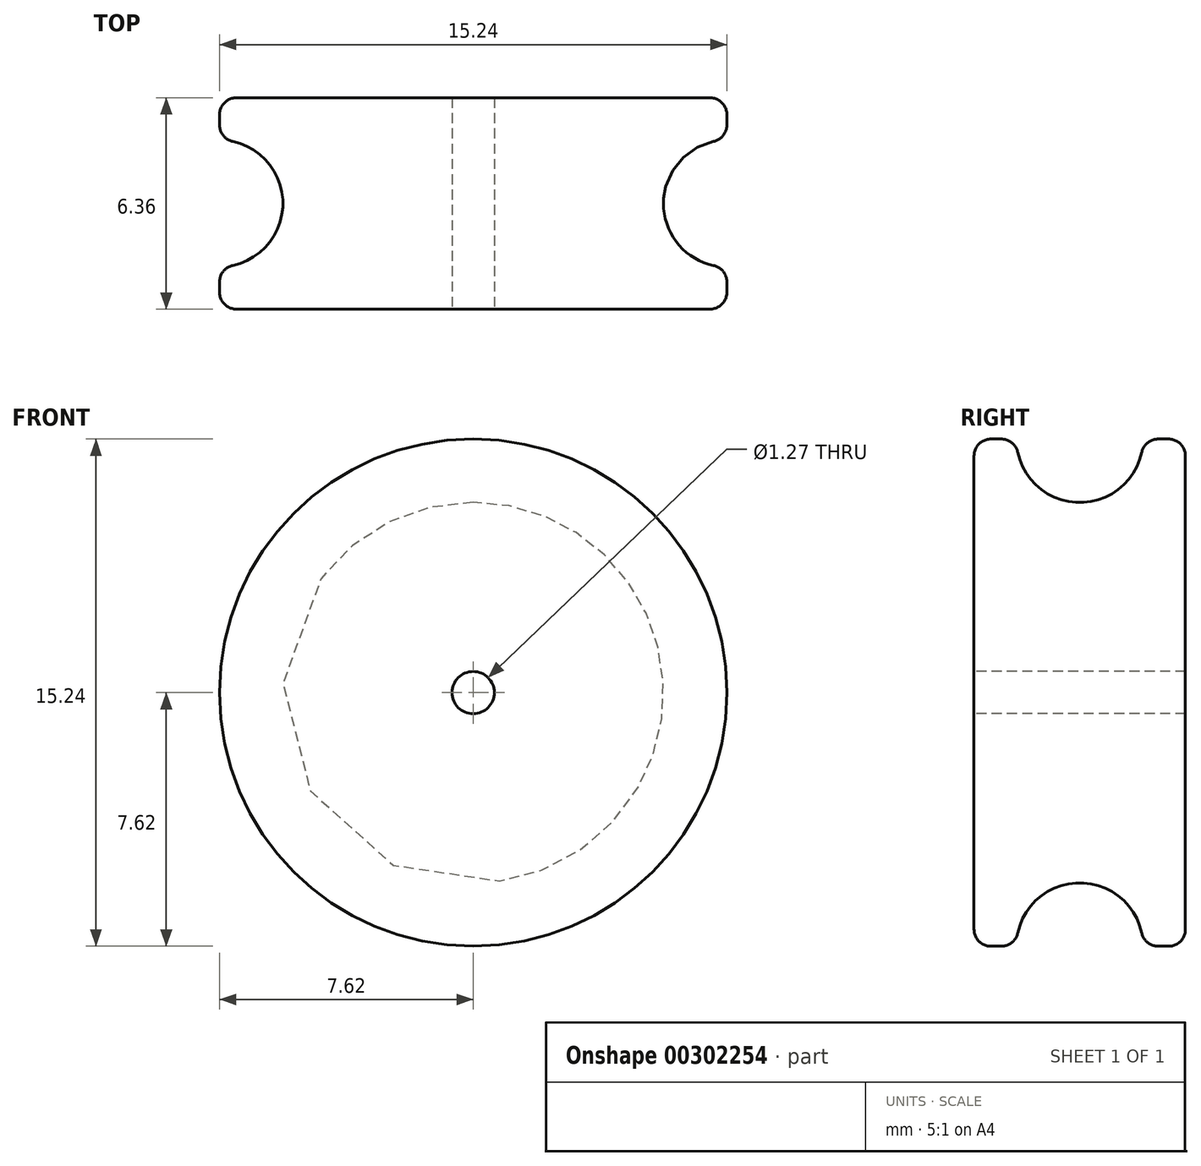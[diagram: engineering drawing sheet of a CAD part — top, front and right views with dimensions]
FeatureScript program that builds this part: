
annotation { "Feature Type Name" : "Feature", "Feature Type Description" : "" }
export const myFeature = defineFeature(function(context is Context, id is Id, definition is map)
    precondition{}
    {
        {
            var Q0;
            Q0=qCreatedBy(makeId("Front.planeOp"),FACE);
            var sketch = newSketch(context, id + "F0", { "sketchPlane" : qUnion([Q0])});
            skCircle(sketch, "E0", {"center": v(0, 0) * mm, "radius": 7.62 * mm});
            skSolve(sketch);
        }
        {
            var Q0;
            Q0 = qSketchRegion(id + "F0", true);
            extrude(context, id + "F1", {"entities" : qUnion([Q0]), "endBound" : BoundingType.SYMMETRIC, "depth" : 6.35 * mm});
        }
        {
            var Q0;
            Q0=qCreatedBy(makeId("Right.planeOp"),FACE);
            var sketch = newSketch(context, id + "F2", { "sketchPlane" : qUnion([Q0])});
            skLineSegment(sketch, "E1", {"start": v(0, 12.44) * mm, "end": v(0, -12.04) * mm, "construction": true});
            skCircle(sketch, "E2", {"center": v(0, 7.62) * mm, "radius": 1.9 * mm});
            skLineSegment(sketch, "E3", {"start": v(-14.4, 0) * mm, "end": v(19.17, 0) * mm, "construction": true});
            skSolve(sketch);
        }
        {
            var Q0;
            Q0 = qSketchRegion(id + "F2", true);
            var Q1;
            Q1=sQuery(id+"F2.wireOp",EDGE,"E3");
            revolve(context, id + "F3", {"operationType" : NewBodyOperationType.REMOVE, "entities" : qUnion([Q0]), "axis" : qUnion([Q1]), "revolveType" : RevolveType.FULL, "oppositeDirection" : true});
        }
        {
            var Q0;
            Q0=makeQuery(id+"F3.boolean.opBoolean","INTERSECT",EDGE,{"disambiguationData":[OD(1.0)],"derivedFrom":[makeQuery(id+"F1.opExtrude","SWEPT_FACE",FACE,{"disambiguationData":[OSD([sQuery(id+"F0.wireOp",EDGE,"E0")])]}),makeQuery(id+"F3.opRevolve","SWEPT_FACE",FACE,{"disambiguationData":[OSD([sQuery(id+"F2.wireOp",EDGE,"E2")])]})]});
            var Q1;
            Q1=makeQuery(id+"F3.boolean.opBoolean","INTERSECT",EDGE,{"disambiguationData":[OD(0.0)],"derivedFrom":[makeQuery(id+"F1.opExtrude","SWEPT_FACE",FACE,{"disambiguationData":[OSD([sQuery(id+"F0.wireOp",EDGE,"E0")])]}),makeQuery(id+"F3.opRevolve","SWEPT_FACE",FACE,{"disambiguationData":[OSD([sQuery(id+"F2.wireOp",EDGE,"E2")])]})]});
            var Q2;
            Q2=makeQuery(id+"F1.opExtrude","CAP_EDGE",EDGE,{"disambiguationData":[OSD([sQuery(id+"F0.wireOp",EDGE,"E0")])],"isStart":false});
            var Q3;
            Q3=makeQuery(id+"F1.opExtrude","CAP_EDGE",EDGE,{"disambiguationData":[OSD([sQuery(id+"F0.wireOp",EDGE,"E0")])],"isStart":true});
            fillet(context, id + "F4", {"entities" : qUnion([Q0, Q1, Q2, Q3]), "radius" : 0.5 * mm, "tangentPropagation" : true, "allowEdgeOverflow" : false});
        }
        {
            var Q0;
            Q0=makeQuery(id+"F1.opExtrude","CAP_FACE",FACE,{"disambiguationData":[OSD([sQuery(id+"F0.wireOp",EDGE,"E0")])],"isStart":false});
            var sketch = newSketch(context, id + "F5", { "sketchPlane" : qUnion([Q0])});
            skCircle(sketch, "E4", {"center": v(0, 0) * mm, "radius": 0.64 * mm});
            skSolve(sketch);
        }
        {
            var Q0;
            Q0 = qSketchRegion(id + "F5", true);
            var Q1;
            Q1=makeQuery(id+"F1.opExtrude","CAP_FACE",FACE,{"disambiguationData":[OSD([sQuery(id+"F0.wireOp",EDGE,"E0")])],"isStart":true});
            extrude(context, id + "F6", {"entities" : qUnion([Q0]), "operationType" : NewBodyOperationType.REMOVE, "endBound" : BoundingType.UP_TO_SURFACE, "oppositeDirection" : true, "endBoundEntityFace" : qUnion([Q1]), "depth" : 25.4 * mm});
        }
    });
